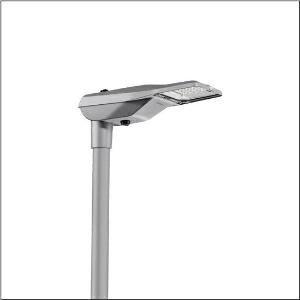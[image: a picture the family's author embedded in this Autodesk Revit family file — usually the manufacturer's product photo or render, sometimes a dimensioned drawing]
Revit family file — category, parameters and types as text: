
# Revit family: streetlight_sl_21_iq_micro___stw1_0a_5xe1e31y08db_aea3
name_source: partatom
category: Lighting Fixtures
units: mm (PartAtom-declared; Revit-internal decimal feet)

## family parameters
Cut with Voids When Loaded = No
Host = Face
Light Source = No
Part Type = Normal
Room Calculation Point = No
Round Connector Dimension = Use Diameter
Shared = No

## types (1)
- --- (1 x LED, 5110 lm, 39.1 W, 3000K)
    Apparent Load = 39 VA
    CIE Flux Codes = 38 75 98 100 100
    Color Rendering = 70
    Color Temperature = 3000K
    Default Elevation = 1800 mm
    Description = Streetlight SL 21 iQ micro, mast luminaire, primary light control with lens, of PMMA, primary optical cover: cover, of toughened safety glass, transparent, light distribution: STW1.0a, light emission: direct distribution, primary light characteristic: asymmetric, installation type: post-top, side-entry, LED, High Power LED, rated luminous flux: 5.110lm, luminous efficacy: 131lm/W, light colour: 730, colour temperature: 3000K, control: pre-setting: logarithmic dimming characteristic, Street-Remote, Auto-Match, Temp-Guard, Lumen-Switch, Night-Set, Smart-Wire, Light-Fading, Desk-Remote (wireless, voltage-free reading and setting of iQ features in the workshop via application-optimized NFC function/RFID function), optimised constant luminous flux control (CLO 2.0), mains connection: 220..240V, AC, 50/60Hz, start of lifetime: 39W, end of service life: 41W, reduction: 17W, luminaire housing, of diecast aluminium, powder-coated, Siteco® metallic grey (DB 702S), corrosivity category C5 mid according to DIN EN ISO 12944, please order mast flange separately, inclination adjustable: 0°, 5°, 10°, 15°, sealing non-destructively replaceable, multi-level sealing system, length: 528mm, width: 235mm, height: 110mm, mast flange for spigot size: 42mm (side-entry): 5XC10008XM4, 60/48mm (side-entry/post-top): 5XC10108XM2, 76/60mm (side-entry/post-top): 5XC10108XM1, Smart Interface below and above, protection rating (complete): IP66, insulation class (complete): insulation class II (safety insulation), certification: CE, ENEC, ENEC+, VDE, impact resistance: IK09, permissible operating ambient temperature for outdoor applications: -40..+50°C, standard-compliant lighting for roads and squares, packaging unit: 1 piece

Light Distribution: STW1.0a
    Height = 110 mm
    Lamp = 1 x LED
    Lamp Light Flux = 5110 lm
    Lamp Power = 39.1 W
    Lamp count = 1
    Length = 528 mm
    Luminous efficacy = 131 lm/W
    Manufacturer = Siteco
    ModVariant = No
    Model = 5XE1E31Y08DB
    Number of Poles = 1
    OnlyDefault = Yes
    Power Factor = 1
    Product Name = Streetlight SL 21 iQ micro | STW1.0a
    Product group = mast luminaire | pylon top
    ProductGroupID = 6100
    Protection Class = Protection class II
    Protection Degree = IP 66
    RLX_Detail_Level = 1
    RLX_Emergency_Light_Flux = 0 lm
    RLX_Emergency_Type = 0
    RLX_Emergency_Type_DB = No
    RlxData = <blob elided: 98793 chars, md5=c7727913>
    Socket = socket
    Standby Power = 0 W
    System Light Flux = 5110 lm
    System Power = 39 W
    Type Comments = factory setting: luminous flux: 100 % | dim-lin: 254 | 765 mA
    Type Image = l_1007239.jpg
    URL = http://relux.com
    VarID = @adj_083225
    Voltage = 0 V
    Weight = 0.00 kg
    Width = 235 mm

## geometry (parser evidence)
native form markers: Blend x4, Sweep x11
no freeform markers — native parametric forms only
